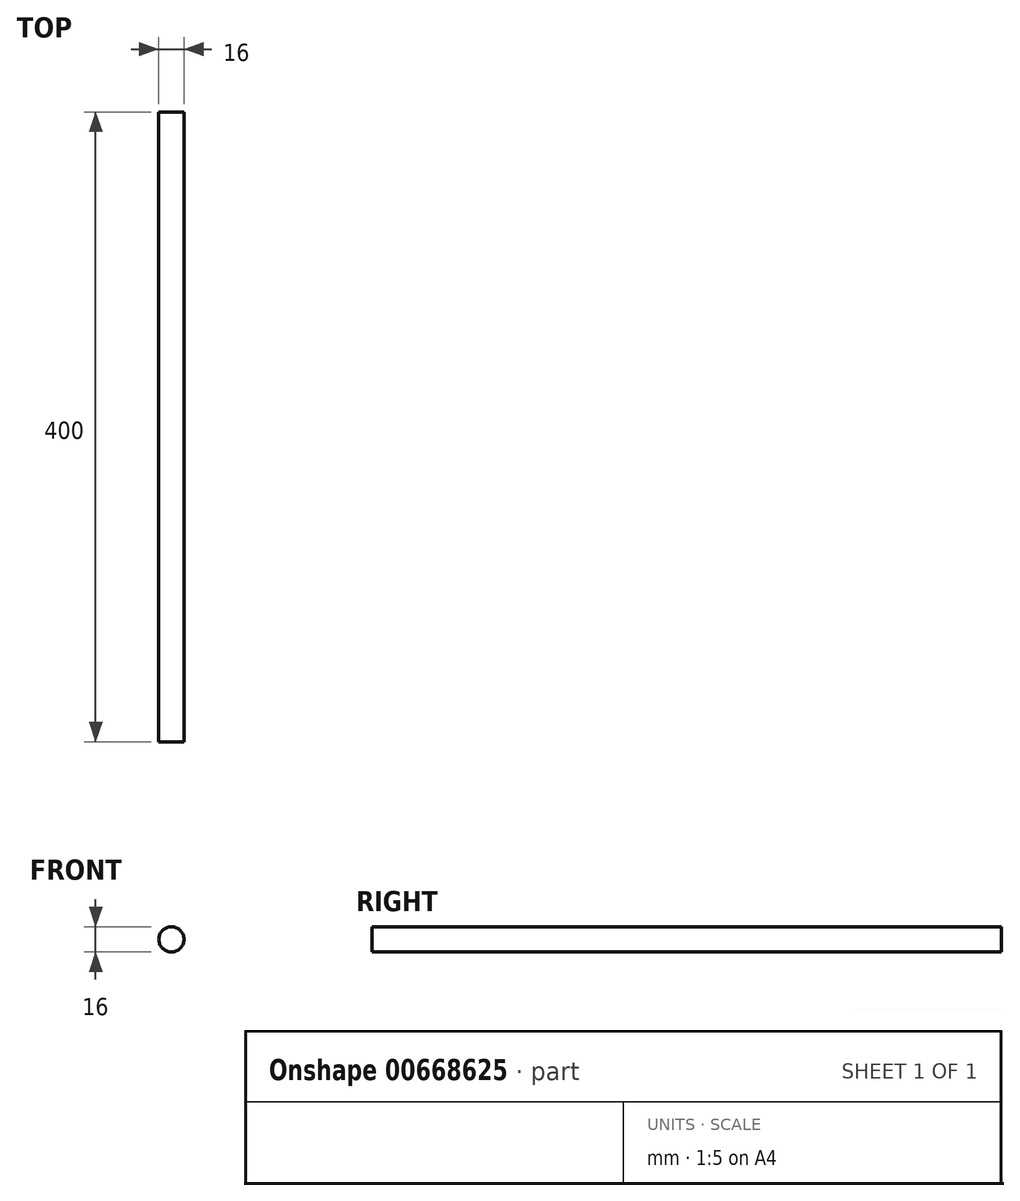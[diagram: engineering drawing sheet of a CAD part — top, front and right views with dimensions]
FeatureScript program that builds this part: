
annotation { "Feature Type Name" : "Feature", "Feature Type Description" : "" }
export const myFeature = defineFeature(function(context is Context, id is Id, definition is map)
    precondition{}
    {
        {
            assignVariable(context, id + "F0", {"name" : "Shaft_length", "anyValue" : 400 * mm});
        }
        {
            var Q0;
            Q0=qCreatedBy(makeId("Front.planeOp"),FACE);
            var sketch = newSketch(context, id + "F1", { "sketchPlane" : qUnion([Q0])});
            skCircle(sketch, "E0", {"center": v(0, 0) * mm, "radius": 8 * mm});
            skSolve(sketch);
        }
        {
            var Q0;
            Q0=qSketchRegion(id+"F1",true);
            extrude(context, id + "F2", {"entities" : qUnion([Q0]), "oppositeDirection" : true, "depth" : getVariable(context, 'Shaft_length')});
        }
    });
